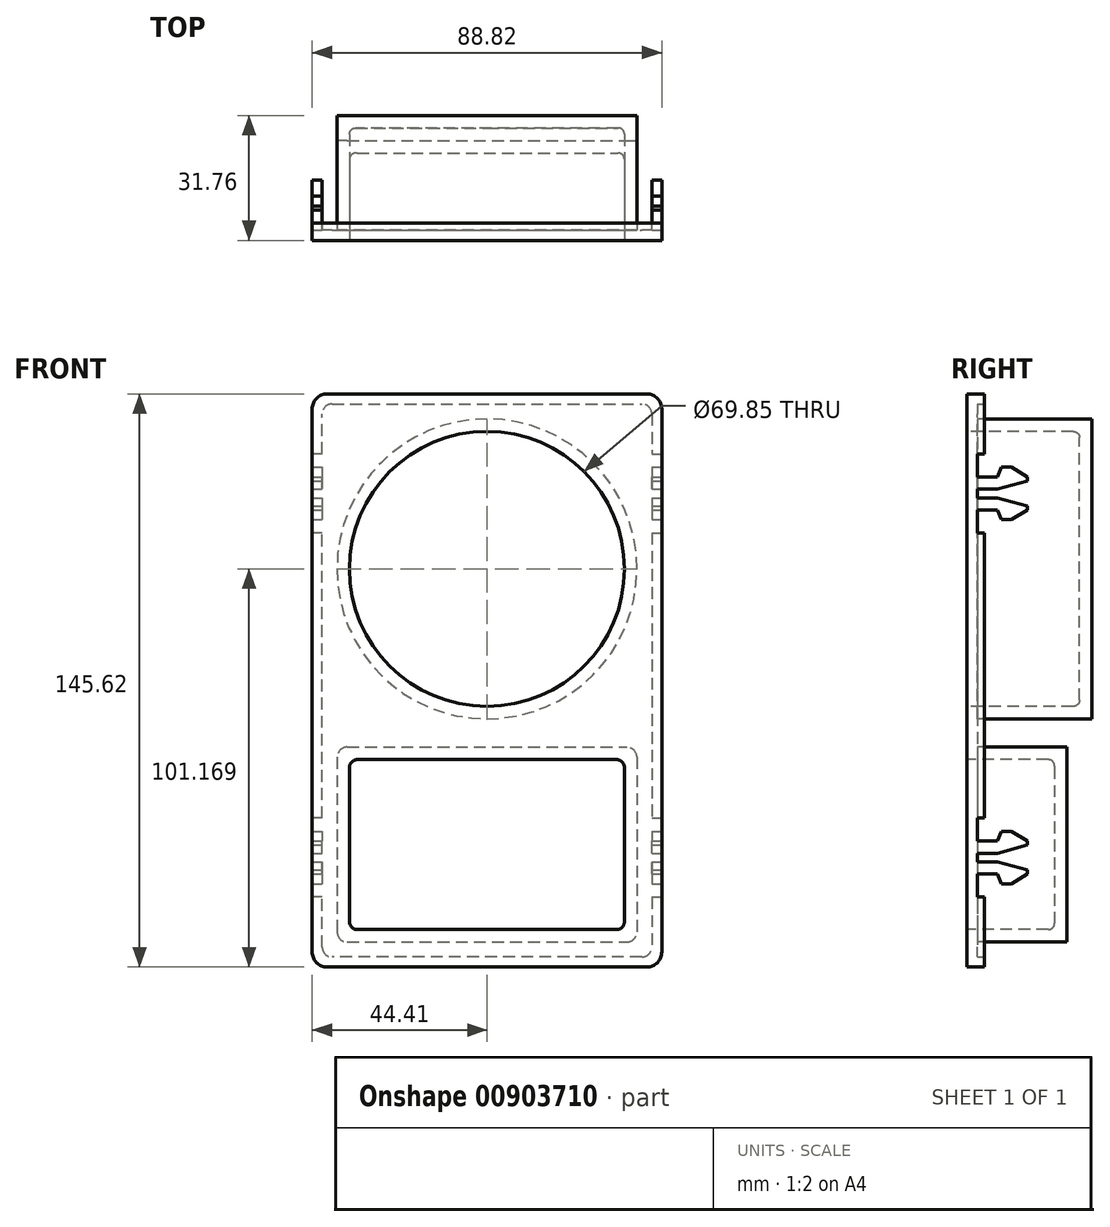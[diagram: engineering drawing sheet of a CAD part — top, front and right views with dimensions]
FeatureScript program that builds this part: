
annotation { "Feature Type Name" : "Feature", "Feature Type Description" : "" }
export const myFeature = defineFeature(function(context is Context, id is Id, definition is map)
    precondition{}
    {
        {
            var Q0;
            Q0=qCreatedBy(makeId("Front.planeOp"),FACE);
            var sketch = newSketch(context, id + "F0", { "sketchPlane" : qUnion([Q0])});
            skLineSegment(sketch, "E0.bottom", {"start": v(-40.6, 72.8) * mm, "end": v(40.6, 72.8) * mm});
            skLineSegment(sketch, "E0.top", {"start": v(-40.6, -72.8) * mm, "end": v(40.6, -72.8) * mm});
            skLineSegment(sketch, "E0.left", {"start": v(-44.41, 69) * mm, "end": v(-44.41, -69) * mm});
            skLineSegment(sketch, "E0.right", {"start": v(44.41, 69) * mm, "end": v(44.41, -69) * mm});
            skPoint(sketch, "E0.middle", {"position": v(0, 0) * mm});
            skPoint(sketch, "E1.visualSharp", {"position": v(-44.41, -72.8) * mm});
            skArc(sketch, "E1.filletArc", {"start": v(-44.41, -69) * mm, "mid": v(-43.3, -71.7) * mm, "end": v(-40.6, -72.8) * mm});
            skPoint(sketch, "E2.visualSharp", {"position": v(44.41, -72.8) * mm});
            skArc(sketch, "E2.filletArc", {"start": v(40.6, -72.8) * mm, "mid": v(43.3, -71.7) * mm, "end": v(44.41, -69) * mm});
            skPoint(sketch, "E3.visualSharp", {"position": v(44.41, 72.8) * mm});
            skArc(sketch, "E3.filletArc", {"start": v(44.41, 69) * mm, "mid": v(43.3, 71.7) * mm, "end": v(40.6, 72.8) * mm});
            skPoint(sketch, "E4.visualSharp", {"position": v(-44.41, 72.8) * mm});
            skArc(sketch, "E4.filletArc", {"start": v(-40.6, 72.8) * mm, "mid": v(-43.3, 71.7) * mm, "end": v(-44.41, 69) * mm});
            skSolve(sketch);
        }
        {
            var Q0;
            Q0=makeQuery(id+"F0.imprint","IMPRINT",FACE,{"disambiguationData":[TD([[makeQuery(id+"F0.imprint","IMPRINT",EDGE,{"derivedFrom":sQuery(id+"F0.wireOp",EDGE,"E0.bottom")}),-1.0]])]});
            extrude(context, id + "F1", {"entities" : qUnion([Q0]), "depth" : 4.44 * mm, "offsetDistance" : 25.4 * mm});
        }
        {
            var Q0;
            Q0=makeQuery(id+"F0.imprint","IMPRINT",FACE,{"disambiguationData":[TD([[makeQuery(id+"F0.imprint","IMPRINT",EDGE,{"derivedFrom":sQuery(id+"F0.wireOp",EDGE,"E0.bottom")}),-1.0]])]});
            var sketch = newSketch(context, id + "F2", { "sketchPlane" : qUnion([Q0])});
            skLineSegment(sketch, "E5", {"start": v(41.87, 67.73) * mm, "end": v(41.87, -67.73) * mm});
            skLineSegment(sketch, "E6", {"start": v(39.33, -70.27) * mm, "end": v(-39.33, -70.27) * mm});
            skLineSegment(sketch, "E7", {"start": v(-41.87, -67.73) * mm, "end": v(-41.87, 67.73) * mm});
            skLineSegment(sketch, "E8", {"start": v(-39.33, 70.27) * mm, "end": v(39.33, 70.27) * mm});
            skPoint(sketch, "E9.visualSharp", {"position": v(41.87, 70.27) * mm});
            skArc(sketch, "E9.filletArc", {"start": v(41.87, 67.73) * mm, "mid": v(41.13, 69.53) * mm, "end": v(39.33, 70.27) * mm});
            skPoint(sketch, "E10.visualSharp", {"position": v(-41.87, 70.27) * mm});
            skArc(sketch, "E10.filletArc", {"start": v(-39.33, 70.27) * mm, "mid": v(-41.13, 69.53) * mm, "end": v(-41.87, 67.73) * mm});
            skPoint(sketch, "E11.visualSharp", {"position": v(-41.87, -70.27) * mm});
            skArc(sketch, "E11.filletArc", {"start": v(-41.87, -67.73) * mm, "mid": v(-41.13, -69.53) * mm, "end": v(-39.33, -70.27) * mm});
            skPoint(sketch, "E12.visualSharp", {"position": v(41.87, -70.27) * mm});
            skArc(sketch, "E12.filletArc", {"start": v(39.33, -70.27) * mm, "mid": v(41.13, -69.53) * mm, "end": v(41.87, -67.73) * mm});
            skSolve(sketch);
        }
        {
            var Q0;
            Q0=qSketchRegion(id+"F2",true);
            extrude(context, id + "F3", {"entities" : qUnion([Q0]), "operationType" : NewBodyOperationType.REMOVE, "depth" : 1.78 * mm, "offsetDistance" : 25.4 * mm});
        }
        {
            var Q0;
            Q0=makeQuery(id+"F1.opExtrude","CAP_FACE",FACE,{"disambiguationData":[OSD([sQuery(id+"F0.wireOp",EDGE,"E0.bottom"),sQuery(id+"F0.wireOp",EDGE,"E0.top"),sQuery(id+"F0.wireOp",EDGE,"E0.left"),sQuery(id+"F0.wireOp",EDGE,"E0.right"),sQuery(id+"F0.wireOp",EDGE,"E1.filletArc"),sQuery(id+"F0.wireOp",EDGE,"E2.filletArc"),sQuery(id+"F0.wireOp",EDGE,"E3.filletArc"),sQuery(id+"F0.wireOp",EDGE,"E4.filletArc")])],"isStart":false});
            var sketch = newSketch(context, id + "F4", { "sketchPlane" : qUnion([Q0])});
            skCircle(sketch, "E13", {"center": v(0, 28.36) * mm, "radius": 34.93 * mm});
            skSolve(sketch);
        }
        {
            var Q0;
            Q0=makeQuery(id+"F4.imprint","IMPRINT",FACE,{"disambiguationData":[TD([[makeQuery(id+"F4.imprint","IMPRINT",EDGE,{"derivedFrom":sQuery(id+"F4.wireOp",EDGE,"E13")}),-1.0]])]});
            var sketch = newSketch(context, id + "F5", { "sketchPlane" : qUnion([Q0])});
            skCircle(sketch, "E14", {"center": v(0, 28.36) * mm, "radius": 38.1 * mm});
            skSolve(sketch);
        }
        {
            var Q0;
            Q0=qSketchRegion(id+"F5",true);
            extrude(context, id + "F6", {"entities" : qUnion([Q0]), "operationType" : NewBodyOperationType.ADD, "oppositeDirection" : true, "depth" : 31.75 * mm, "offsetDistance" : 25.4 * mm});
        }
        {
            var Q0;
            Q0=qSketchRegion(id+"F4",true);
            extrude(context, id + "F7", {"entities" : qUnion([Q0]), "operationType" : NewBodyOperationType.REMOVE, "oppositeDirection" : true, "depth" : 28.57 * mm, "offsetDistance" : 25.4 * mm});
        }
        {
            var Q0;
            Q0=makeQuery(id+"F1.opExtrude","CAP_FACE",FACE,{"disambiguationData":[OSD([sQuery(id+"F0.wireOp",EDGE,"E0.bottom"),sQuery(id+"F0.wireOp",EDGE,"E0.top"),sQuery(id+"F0.wireOp",EDGE,"E0.left"),sQuery(id+"F0.wireOp",EDGE,"E0.right"),sQuery(id+"F0.wireOp",EDGE,"E1.filletArc"),sQuery(id+"F0.wireOp",EDGE,"E2.filletArc"),sQuery(id+"F0.wireOp",EDGE,"E3.filletArc"),sQuery(id+"F0.wireOp",EDGE,"E4.filletArc")])],"isStart":false});
            var sketch = newSketch(context, id + "F8", { "sketchPlane" : qUnion([Q0])});
            skLineSegment(sketch, "E15.bottom", {"start": v(-35.52, -16.93) * mm, "end": v(35.52, -16.93) * mm});
            skLineSegment(sketch, "E15.top", {"start": v(-35.52, -66.46) * mm, "end": v(35.52, -66.46) * mm});
            skLineSegment(sketch, "E15.left", {"start": v(-38.06, -19.47) * mm, "end": v(-38.06, -63.92) * mm});
            skLineSegment(sketch, "E15.right", {"start": v(38.06, -19.47) * mm, "end": v(38.06, -63.92) * mm});
            skPoint(sketch, "E15.middle", {"position": v(0, -41.7) * mm});
            skPoint(sketch, "E16.visualSharp", {"position": v(-38.06, -16.93) * mm});
            skArc(sketch, "E16.filletArc", {"start": v(-35.52, -16.93) * mm, "mid": v(-37.32, -17.67) * mm, "end": v(-38.06, -19.47) * mm});
            skPoint(sketch, "E17.visualSharp", {"position": v(38.06, -16.93) * mm});
            skArc(sketch, "E17.filletArc", {"start": v(38.06, -19.47) * mm, "mid": v(37.32, -17.67) * mm, "end": v(35.52, -16.93) * mm});
            skPoint(sketch, "E18.visualSharp", {"position": v(-38.06, -66.46) * mm});
            skArc(sketch, "E18.filletArc", {"start": v(-38.06, -63.92) * mm, "mid": v(-37.32, -65.72) * mm, "end": v(-35.52, -66.46) * mm});
            skPoint(sketch, "E19.visualSharp", {"position": v(38.06, -66.46) * mm});
            skArc(sketch, "E19.filletArc", {"start": v(35.52, -66.46) * mm, "mid": v(37.32, -65.72) * mm, "end": v(38.06, -63.92) * mm});
            skSolve(sketch);
        }
        {
            var Q0;
            Q0=makeQuery(id+"F8.imprint","IMPRINT",FACE,{"disambiguationData":[TD([[makeQuery(id+"F8.imprint","IMPRINT",EDGE,{"derivedFrom":sQuery(id+"F8.wireOp",EDGE,"E15.bottom")}),1.0]])]});
            var sketch = newSketch(context, id + "F9", { "sketchPlane" : qUnion([Q0])});
            skLineSegment(sketch, "E20.bottom", {"start": v(-32.98, -20.1) * mm, "end": v(32.98, -20.1) * mm});
            skLineSegment(sketch, "E20.top", {"start": v(-32.98, -63.28) * mm, "end": v(32.98, -63.28) * mm});
            skLineSegment(sketch, "E20.left", {"start": v(-34.89, -22) * mm, "end": v(-34.89, -61.38) * mm});
            skLineSegment(sketch, "E20.right", {"start": v(34.89, -22) * mm, "end": v(34.89, -61.38) * mm});
            skPoint(sketch, "E20.middle", {"position": v(0, -41.7) * mm});
            skPoint(sketch, "E21.visualSharp", {"position": v(-34.89, -20.1) * mm});
            skArc(sketch, "E21.filletArc", {"start": v(-32.98, -20.1) * mm, "mid": v(-34.33, -20.66) * mm, "end": v(-34.89, -22) * mm});
            skPoint(sketch, "E22.visualSharp", {"position": v(34.89, -20.1) * mm});
            skArc(sketch, "E22.filletArc", {"start": v(34.89, -22) * mm, "mid": v(34.33, -20.66) * mm, "end": v(32.98, -20.1) * mm});
            skPoint(sketch, "E23.visualSharp", {"position": v(-34.89, -63.28) * mm});
            skArc(sketch, "E23.filletArc", {"start": v(-34.89, -61.38) * mm, "mid": v(-34.33, -62.73) * mm, "end": v(-32.98, -63.28) * mm});
            skPoint(sketch, "E24.visualSharp", {"position": v(34.89, -63.28) * mm});
            skArc(sketch, "E24.filletArc", {"start": v(32.98, -63.28) * mm, "mid": v(34.33, -62.73) * mm, "end": v(34.89, -61.38) * mm});
            skSolve(sketch);
        }
        {
            var Q0;
            Q0=qSketchRegion(id+"F8",true);
            extrude(context, id + "F10", {"entities" : qUnion([Q0]), "operationType" : NewBodyOperationType.ADD, "oppositeDirection" : true, "depth" : 25.4 * mm, "offsetDistance" : 25.4 * mm});
        }
        {
            var Q0;
            Q0=qSketchRegion(id+"F9",true);
            extrude(context, id + "F11", {"entities" : qUnion([Q0]), "operationType" : NewBodyOperationType.REMOVE, "oppositeDirection" : true, "depth" : 22.22 * mm, "offsetDistance" : 25.4 * mm});
        }
        {
            var Q0;
            Q0=makeQuery(id+"F11.boolean.opBoolean","COPY",FACE,{"derivedFrom":makeQuery(id+"F11.opExtrude","CAP_FACE",FACE,{"disambiguationData":[OSD([sQuery(id+"F9.wireOp",EDGE,"E20.bottom"),sQuery(id+"F9.wireOp",EDGE,"E20.top"),sQuery(id+"F9.wireOp",EDGE,"E20.left"),sQuery(id+"F9.wireOp",EDGE,"E20.right"),sQuery(id+"F9.wireOp",EDGE,"E21.filletArc"),sQuery(id+"F9.wireOp",EDGE,"E22.filletArc"),sQuery(id+"F9.wireOp",EDGE,"E23.filletArc"),sQuery(id+"F9.wireOp",EDGE,"E24.filletArc")])],"isStart":false})});
            var Q1;
            Q1=makeQuery(id+"F7.boolean.opBoolean","COPY",FACE,{"derivedFrom":makeQuery(id+"F7.opExtrude","CAP_FACE",FACE,{"disambiguationData":[OSD([sQuery(id+"F4.wireOp",EDGE,"E13")])],"isStart":false})});
            fillet(context, id + "F12", {"entities" : qUnion([Q0, Q1]), "radius" : 1.59 * mm, "tangentPropagation" : true, "allowEdgeOverflow" : false});
        }
        {
            var Q0;
            Q0=makeQuery(id+"F1.opExtrude","SWEPT_FACE",FACE,{"disambiguationData":[OSD([sQuery(id+"F0.wireOp",EDGE,"E0.right")])]});
            var sketch = newSketch(context, id + "F13", { "sketchPlane" : qUnion([Q0])});
            skLineSegment(sketch, "E25", {"start": v(0, -55.03) * mm, "end": v(-1.78, -55.03) * mm});
            skLineSegment(sketch, "E26", {"start": v(-1.78, -55.03) * mm, "end": v(-1.78, -34.96) * mm});
            skLineSegment(sketch, "E27", {"start": v(-1.78, -34.96) * mm, "end": v(0, -34.96) * mm});
            skLineSegment(sketch, "E28", {"start": v(0, -34.96) * mm, "end": v(0, -55.03) * mm});
            skSolve(sketch);
        }
        {
            var Q0;
            Q0=qSketchRegion(id+"F13",true);
            extrude(context, id + "F14", {"entities" : qUnion([Q0]), "operationType" : NewBodyOperationType.REMOVE, "oppositeDirection" : true, "depth" : 2.54 * mm, "offsetDistance" : 25.4 * mm});
        }
        {
            var Q0;
            Q0=makeQuery(id+"F1.opExtrude","SWEPT_FACE",FACE,{"disambiguationData":[OSD([sQuery(id+"F0.wireOp",EDGE,"E0.left")])]});
            var sketch = newSketch(context, id + "F15", { "sketchPlane" : qUnion([Q0])});
            skLineSegment(sketch, "E29", {"start": v(0, -55.03) * mm, "end": v(1.78, -55.03) * mm});
            skLineSegment(sketch, "E30", {"start": v(1.78, -55.03) * mm, "end": v(1.78, -34.96) * mm});
            skLineSegment(sketch, "E31", {"start": v(1.78, -34.96) * mm, "end": v(0, -34.96) * mm});
            skLineSegment(sketch, "E32", {"start": v(0, -34.96) * mm, "end": v(0, -55.03) * mm});
            skSolve(sketch);
        }
        {
            var Q0;
            Q0=makeQuery(id+"F15.imprint","IMPRINT",FACE,{"disambiguationData":[TD([[makeQuery(id+"F15.imprint","IMPRINT",EDGE,{"derivedFrom":sQuery(id+"F15.wireOp",EDGE,"E29")}),1.0]])]});
            extrude(context, id + "F16", {"entities" : qUnion([Q0]), "operationType" : NewBodyOperationType.REMOVE, "oppositeDirection" : true, "depth" : 2.54 * mm, "offsetDistance" : 25.4 * mm});
        }
        {
            var Q0;
            Q0=makeQuery(id+"F1.opExtrude","SWEPT_FACE",FACE,{"disambiguationData":[OSD([sQuery(id+"F0.wireOp",EDGE,"E0.right")])]});
            var sketch = newSketch(context, id + "F17", { "sketchPlane" : qUnion([Q0])});
            skLineSegment(sketch, "E33", {"start": v(0, 57.57) * mm, "end": v(-1.78, 57.57) * mm});
            skLineSegment(sketch, "E34", {"start": v(-1.78, 57.57) * mm, "end": v(-1.78, 37.5) * mm});
            skLineSegment(sketch, "E35", {"start": v(-1.78, 37.5) * mm, "end": v(0, 37.5) * mm});
            skLineSegment(sketch, "E36", {"start": v(0, 37.5) * mm, "end": v(0, 57.57) * mm});
            skSolve(sketch);
        }
        {
            var Q0;
            Q0=qSketchRegion(id+"F17",true);
            extrude(context, id + "F18", {"entities" : qUnion([Q0]), "operationType" : NewBodyOperationType.REMOVE, "oppositeDirection" : true, "depth" : 2.54 * mm, "offsetDistance" : 25.4 * mm});
        }
        {
            var Q0;
            Q0=makeQuery(id+"F1.opExtrude","SWEPT_FACE",FACE,{"disambiguationData":[OSD([sQuery(id+"F0.wireOp",EDGE,"E0.left")])]});
            var sketch = newSketch(context, id + "F19", { "sketchPlane" : qUnion([Q0])});
            skLineSegment(sketch, "E37", {"start": v(0, 57.57) * mm, "end": v(1.78, 57.57) * mm});
            skLineSegment(sketch, "E38", {"start": v(1.78, 57.57) * mm, "end": v(1.78, 37.5) * mm});
            skLineSegment(sketch, "E39", {"start": v(1.78, 37.5) * mm, "end": v(0, 37.5) * mm});
            skLineSegment(sketch, "E40", {"start": v(0, 37.5) * mm, "end": v(0, 57.57) * mm});
            skSolve(sketch);
        }
        {
            var Q0;
            Q0=qSketchRegion(id+"F19",true);
            extrude(context, id + "F20", {"entities" : qUnion([Q0]), "operationType" : NewBodyOperationType.REMOVE, "oppositeDirection" : true, "depth" : 2.54 * mm, "offsetDistance" : 25.4 * mm});
        }
        {
            var Q0;
            Q0=makeQuery(id+"F1.opExtrude","SWEPT_FACE",FACE,{"disambiguationData":[OSD([sQuery(id+"F0.wireOp",EDGE,"E0.right")])]});
            var sketch = newSketch(context, id + "F21", { "sketchPlane" : qUnion([Q0])});
            skLineSegment(sketch, "E41", {"start": v(-1.78, -49.19) * mm, "end": v(3.3, -49.19) * mm});
            skLineSegment(sketch, "E42", {"start": v(-1.78, -46.11) * mm, "end": v(3.32, -46.11) * mm});
            skLineSegment(sketch, "E43", {"start": v(-1.78, -49.19) * mm, "end": v(-1.78, -46.11) * mm});
            skLineSegment(sketch, "E44", {"start": v(-1.78, -43.88) * mm, "end": v(-1.78, -40.8) * mm});
            skLineSegment(sketch, "E45", {"start": v(3.3, -49.19) * mm, "end": v(4.32, -51.66) * mm});
            skLineSegment(sketch, "E46", {"start": v(4.32, -51.66) * mm, "end": v(6.86, -51.66) * mm});
            skLineSegment(sketch, "E47", {"start": v(3.32, -46.11) * mm, "end": v(10.92, -48.17) * mm});
            skLineSegment(sketch, "E48", {"start": v(10.92, -48.17) * mm, "end": v(10.92, -49.19) * mm});
            skLineSegment(sketch, "E49", {"start": v(6.86, -51.66) * mm, "end": v(10.92, -49.19) * mm});
            skLineSegment(sketch, "E50.MirrorCS", {"start": v(-1.78, -43.88) * mm, "end": v(3.32, -43.88) * mm});
            skLineSegment(sketch, "E51.MirrorCS", {"start": v(3.32, -43.88) * mm, "end": v(10.92, -41.82) * mm});
            skLineSegment(sketch, "E52.MirrorCS", {"start": v(10.92, -41.82) * mm, "end": v(10.92, -40.8) * mm});
            skLineSegment(sketch, "E53.MirrorCS", {"start": v(6.86, -38.33) * mm, "end": v(10.92, -40.8) * mm});
            skLineSegment(sketch, "E54.MirrorCS", {"start": v(4.32, -38.33) * mm, "end": v(6.86, -38.33) * mm});
            skLineSegment(sketch, "E55.MirrorCS", {"start": v(3.3, -40.8) * mm, "end": v(4.32, -38.33) * mm});
            skLineSegment(sketch, "E56.MirrorCS", {"start": v(-1.78, -40.8) * mm, "end": v(3.3, -40.8) * mm});
            skLineSegment(sketch, "E57.MirrorCS", {"start": v(-1.78, -40.8) * mm, "end": v(-1.78, -43.88) * mm});
            skLineSegment(sketch, "E58.MirrorCS", {"start": v(-1.78, 43.35) * mm, "end": v(3.3, 43.35) * mm});
            skLineSegment(sketch, "E59.MirrorCS", {"start": v(-1.78, 43.35) * mm, "end": v(-1.78, 46.42) * mm});
            skLineSegment(sketch, "E60.MirrorCS", {"start": v(-1.78, 46.42) * mm, "end": v(3.32, 46.42) * mm});
            skLineSegment(sketch, "E61.MirrorCS", {"start": v(3.32, 46.42) * mm, "end": v(10.92, 44.36) * mm});
            skLineSegment(sketch, "E62.MirrorCS", {"start": v(6.86, 40.87) * mm, "end": v(10.92, 43.35) * mm});
            skLineSegment(sketch, "E63.MirrorCS", {"start": v(10.92, 44.36) * mm, "end": v(10.92, 43.35) * mm});
            skLineSegment(sketch, "E64.MirrorCS", {"start": v(4.32, 40.87) * mm, "end": v(6.86, 40.87) * mm});
            skLineSegment(sketch, "E65.MirrorCS", {"start": v(3.3, 43.35) * mm, "end": v(4.32, 40.87) * mm});
            skLineSegment(sketch, "E66.MirrorCS", {"start": v(-1.78, 51.73) * mm, "end": v(-1.78, 48.65) * mm});
            skLineSegment(sketch, "E67.MirrorCS", {"start": v(-1.78, 48.65) * mm, "end": v(3.32, 48.65) * mm});
            skLineSegment(sketch, "E68.MirrorCS", {"start": v(3.32, 48.65) * mm, "end": v(10.92, 50.71) * mm});
            skLineSegment(sketch, "E69.MirrorCS", {"start": v(10.92, 50.71) * mm, "end": v(10.92, 51.73) * mm});
            skLineSegment(sketch, "E70.MirrorCS", {"start": v(6.86, 54.2) * mm, "end": v(10.92, 51.73) * mm});
            skLineSegment(sketch, "E71.MirrorCS", {"start": v(4.32, 54.2) * mm, "end": v(6.86, 54.2) * mm});
            skLineSegment(sketch, "E72.MirrorCS", {"start": v(3.3, 51.73) * mm, "end": v(4.32, 54.2) * mm});
            skLineSegment(sketch, "E73.MirrorCS", {"start": v(-1.78, 51.73) * mm, "end": v(3.3, 51.73) * mm});
            skSolve(sketch);
        }
        {
            var Q0;
            Q0=qSketchRegion(id+"F21",true);
            extrude(context, id + "F22", {"entities" : qUnion([Q0]), "operationType" : NewBodyOperationType.ADD, "oppositeDirection" : true, "depth" : 2.54 * mm, "offsetDistance" : 25.4 * mm, "hasSecondDirection" : true, "secondDirectionOppositeDirection" : true, "secondDirectionDepth" : 0 * mm});
        }
        {
            var Q0;
            Q0=qSketchRegion(id+"F21",true);
            extrude(context, id + "F23", {"entities" : qUnion([Q0]), "operationType" : NewBodyOperationType.ADD, "oppositeDirection" : true, "depth" : 88.82 * mm, "offsetDistance" : 25.4 * mm, "hasSecondDirection" : true, "secondDirectionOppositeDirection" : true, "secondDirectionDepth" : 86.28 * mm});
        }
    });
